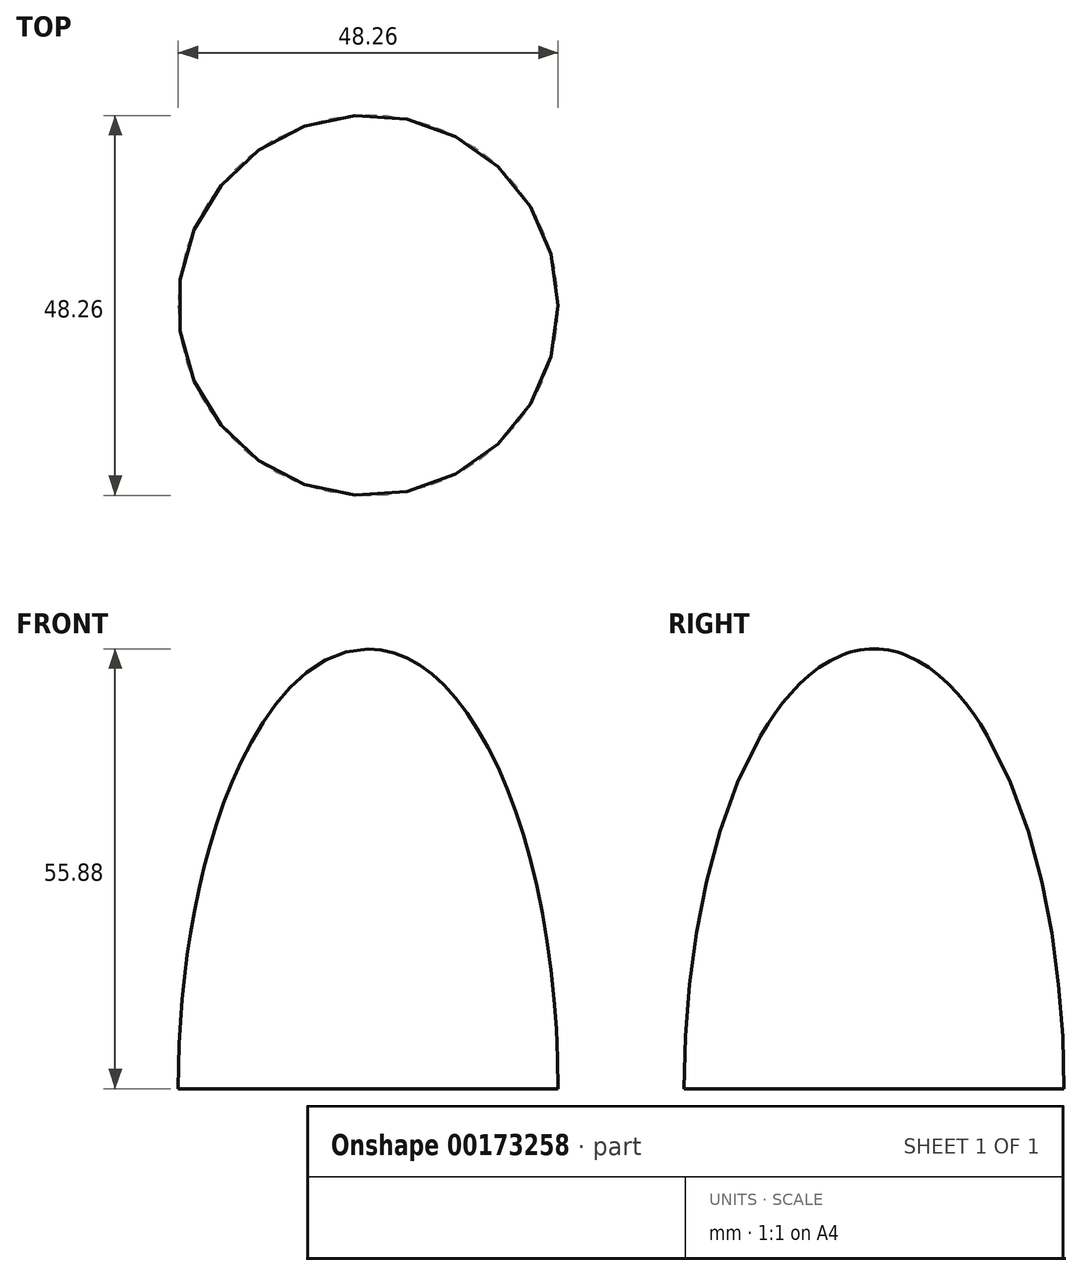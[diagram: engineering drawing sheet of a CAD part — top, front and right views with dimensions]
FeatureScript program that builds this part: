
annotation { "Feature Type Name" : "Feature", "Feature Type Description" : "" }
export const myFeature = defineFeature(function(context is Context, id is Id, definition is map)
    precondition{}
    {
        {
            var Q0;
            Q0=qCreatedBy(makeId("Front.planeOp"),FACE);
            var sketch = newSketch(context, id + "F0", { "sketchPlane" : qUnion([Q0])});
            skLineSegment(sketch, "E0", {"start": v(-27.4, 0) * mm, "end": v(20.86, 0) * mm});
            skEllipticalArc(sketch, "E1", {});
            skLineSegment(sketch, "E2", {"start": v(-3.27, 0) * mm, "end": v(-3.27, 55.88) * mm});
            const initialGuessF0  = {"E1": [-0.003265714577510595, 0, 0, 1, 0.05588, 0.02413, 4.71238898038469, 1.5707963267948966]};
            skSetInitialGuess(sketch, initialGuessF0);
            skSolve(sketch);
        }
        {
            var Q0;
            {var subQ3=sQuery(id+"F0.wireOp",EDGE,"E2");Q0=makeQuery(id+"F0.imprint","IMPRINT",FACE,{"disambiguationData":[TD([[makeQuery(id+"F0.imprint","IMPRINT",EDGE,{"derivedFrom":subQ3}),-1.0]])]});}
            var Q1;
            Q1=sQuery(id+"F0.wireOp",EDGE,"E2");
            revolve(context, id + "F1", {"entities" : qUnion([Q0]), "axis" : qUnion([Q1]), "revolveType" : RevolveType.FULL});
        }
    });
